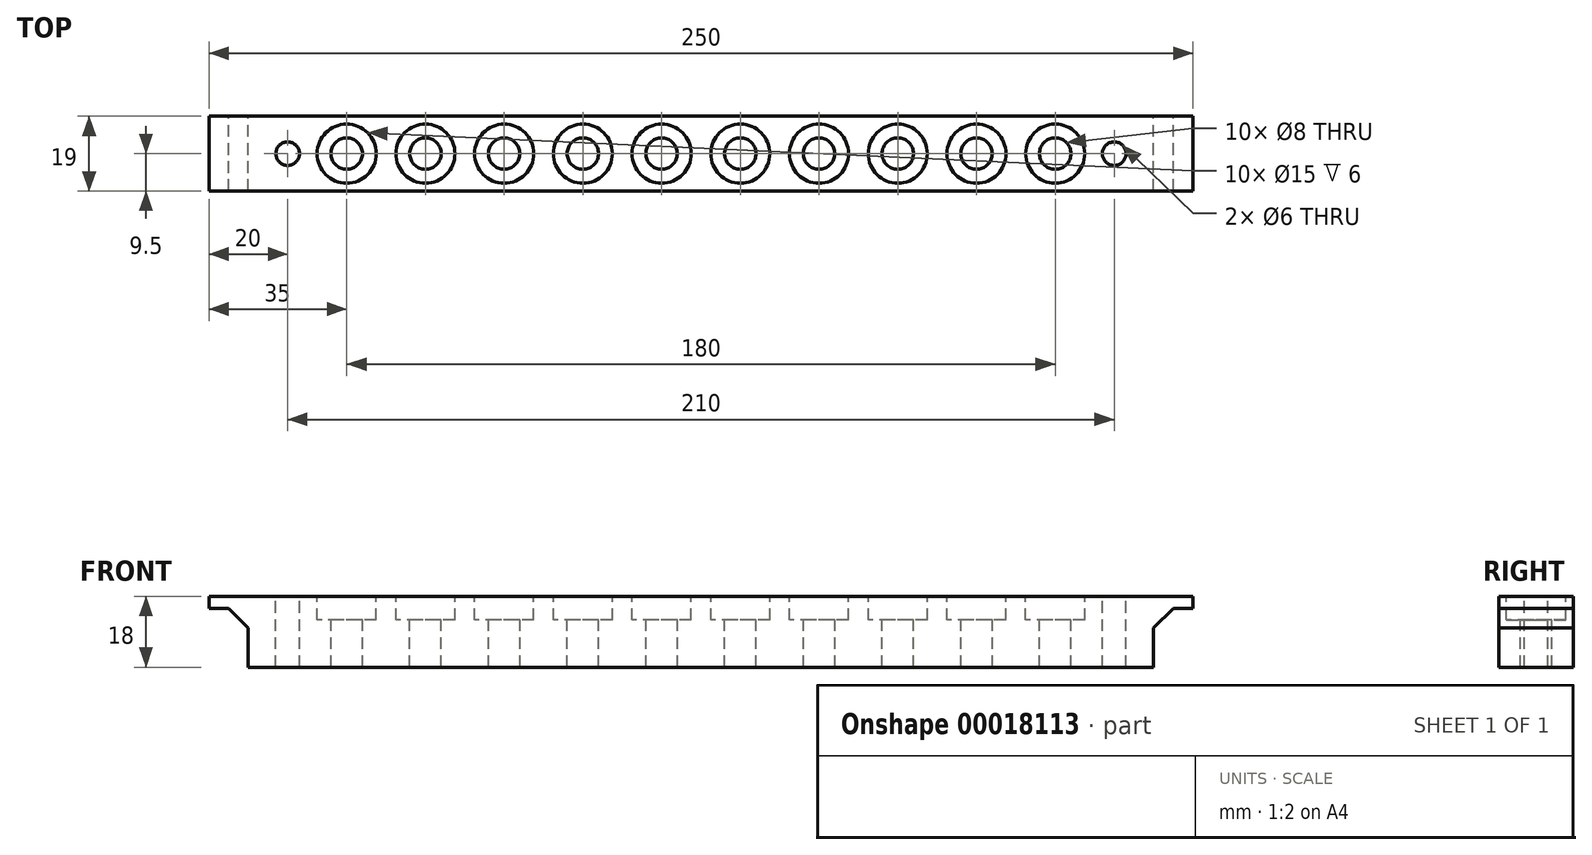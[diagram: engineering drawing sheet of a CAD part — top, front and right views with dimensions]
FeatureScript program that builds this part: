
annotation { "Feature Type Name" : "Feature", "Feature Type Description" : "" }
export const myFeature = defineFeature(function(context is Context, id is Id, definition is map)
    precondition{}
    {
        {
            var Q0;
            Q0=qCreatedBy(makeId("Front.planeOp"),FACE);
            var sketch = newSketch(context, id + "F0", { "sketchPlane" : qUnion([Q0])});
            skLineSegment(sketch, "E0", {"start": v(-125, 9) * mm, "end": v(125, 9) * mm});
            skLineSegment(sketch, "E1", {"start": v(125, 9) * mm, "end": v(125, 6) * mm});
            skLineSegment(sketch, "E2", {"start": v(125, 6) * mm, "end": v(120, 6) * mm});
            skLineSegment(sketch, "E3", {"start": v(115, 1) * mm, "end": v(115, -9) * mm});
            skLineSegment(sketch, "E4", {"start": v(115, -9) * mm, "end": v(-115, -9) * mm});
            skLineSegment(sketch, "E5", {"start": v(120, 6) * mm, "end": v(115, 1) * mm});
            skLineSegment(sketch, "E6", {"start": v(-125, 9) * mm, "end": v(-125, 6) * mm});
            skLineSegment(sketch, "E7", {"start": v(-125, 6) * mm, "end": v(-120, 6) * mm});
            skLineSegment(sketch, "E8", {"start": v(-115, 1) * mm, "end": v(-115, -9) * mm});
            skLineSegment(sketch, "E9", {"start": v(-120, 6) * mm, "end": v(-115, 1) * mm});
            skSolve(sketch);
        }
        {
            var Q0;
            Q0 = qSketchRegion(id + "F0", true);
            extrude(context, id + "F1", {"entities" : qUnion([Q0]), "endBound" : BoundingType.SYMMETRIC, "depth" : 19 * mm});
        }
        {
            var Q0;
            Q0=makeQuery(id+"F1.opExtrude","SWEPT_BODY",BODY,{"disambiguationData":[OSD([sQuery(id+"F0.wireOp",EDGE,"E0"),sQuery(id+"F0.wireOp",EDGE,"E1"),sQuery(id+"F0.wireOp",EDGE,"E2"),sQuery(id+"F0.wireOp",EDGE,"E3"),sQuery(id+"F0.wireOp",EDGE,"E4"),sQuery(id+"F0.wireOp",EDGE,"E5"),sQuery(id+"F0.wireOp",EDGE,"E6"),sQuery(id+"F0.wireOp",EDGE,"E7"),sQuery(id+"F0.wireOp",EDGE,"E8"),sQuery(id+"F0.wireOp",EDGE,"E9")])]});
            transform(context, id + "F2", {"entities" : qUnion([Q0]), "transformType" : TransformType.TRANSLATION_3D, "dx" : 125 * mm, "dy" : 0 * mm, "dz" : 0 * mm, "makeCopy" : false});
        }
        {
            var Q0;
            Q0=makeQuery(id+"F1.opExtrude","SWEPT_FACE",FACE,{"disambiguationData":[OSD([sQuery(id+"F0.wireOp",EDGE,"E0")])]});
            var sketch = newSketch(context, id + "F3", { "sketchPlane" : qUnion([Q0])});
            skLineSegment(sketch, "E10.0", {"start": v(20, -9.5) * mm, "end": v(20, 9.5) * mm, "construction": true});
            skLineSegment(sketch, "E11", {"start": v(-2.51, 0) * mm, "end": v(250, 0) * mm, "construction": true});
            skLineSegment(sketch, "E12.0", {"start": v(230, -9.5) * mm, "end": v(230, 9.5) * mm, "construction": true});
            skLineSegment(sketch, "E13.0", {"start": v(35, -9.5) * mm, "end": v(35, 9.5) * mm, "construction": true});
            skPoint(sketch, "E14", {"position": v(20, 0) * mm});
            skPoint(sketch, "E15", {"position": v(35, 0) * mm});
            skPoint(sketch, "E16", {"position": v(230, 0) * mm});
            skLineSegment(sketch, "E17.1.0.0", {"start": v(55, -9.5) * mm, "end": v(55, 9.5) * mm, "construction": true});
            skPoint(sketch, "E17.1.0.1", {"position": v(55, 0) * mm});
            skLineSegment(sketch, "E17.2.0.0", {"start": v(75, -9.5) * mm, "end": v(75, 9.5) * mm, "construction": true});
            skPoint(sketch, "E17.2.0.1", {"position": v(75, 0) * mm});
            skLineSegment(sketch, "E17.3.0.0", {"start": v(95, -9.5) * mm, "end": v(95, 9.5) * mm, "construction": true});
            skPoint(sketch, "E17.3.0.1", {"position": v(95, 0) * mm});
            skLineSegment(sketch, "E17.4.0.0", {"start": v(115, -9.5) * mm, "end": v(115, 9.5) * mm, "construction": true});
            skPoint(sketch, "E17.4.0.1", {"position": v(115, 0) * mm});
            skLineSegment(sketch, "E17.5.0.0", {"start": v(135, -9.5) * mm, "end": v(135, 9.5) * mm, "construction": true});
            skPoint(sketch, "E17.5.0.1", {"position": v(135, 0) * mm});
            skLineSegment(sketch, "E17.6.0.0", {"start": v(155, -9.5) * mm, "end": v(155, 9.5) * mm, "construction": true});
            skPoint(sketch, "E17.6.0.1", {"position": v(155, 0) * mm});
            skLineSegment(sketch, "E17.7.0.0", {"start": v(175, -9.5) * mm, "end": v(175, 9.5) * mm, "construction": true});
            skPoint(sketch, "E17.7.0.1", {"position": v(175, 0) * mm});
            skLineSegment(sketch, "E17.8.0.0", {"start": v(195, -9.5) * mm, "end": v(195, 9.5) * mm, "construction": true});
            skPoint(sketch, "E17.8.0.1", {"position": v(195, 0) * mm});
            skLineSegment(sketch, "E17.9.0.0", {"start": v(215, -9.5) * mm, "end": v(215, 9.5) * mm, "construction": true});
            skPoint(sketch, "E17.9.0.1", {"position": v(215, 0) * mm});
            skLineSegment(sketch, "E17.direction1", {"start": v(35, -9.5) * mm, "end": v(55, -9.5) * mm, "construction": true});
            skSolve(sketch);
        }
        {
            var Q0;
            Q0=sQuery(id+"F3.wireOp",VERTEX,"E15");
            var Q1;
            Q1=sQuery(id+"F3.wireOp",VERTEX,"E17.1.0.1");
            var Q2;
            Q2=sQuery(id+"F3.wireOp",VERTEX,"E17.2.0.1");
            var Q3;
            Q3=sQuery(id+"F3.wireOp",VERTEX,"E17.3.0.1");
            var Q4;
            Q4=sQuery(id+"F3.wireOp",VERTEX,"E17.4.0.1");
            var Q5;
            Q5=sQuery(id+"F3.wireOp",VERTEX,"E17.5.0.1");
            var Q6;
            Q6=sQuery(id+"F3.wireOp",VERTEX,"E17.6.0.1");
            var Q7;
            Q7=sQuery(id+"F3.wireOp",VERTEX,"E17.7.0.1");
            var Q8;
            Q8=sQuery(id+"F3.wireOp",VERTEX,"E17.8.0.1");
            var Q9;
            Q9=sQuery(id+"F3.wireOp",VERTEX,"E17.9.0.1");
            var Q10;
            Q10=makeQuery(id+"F1.opExtrude","SWEPT_BODY",BODY,{"disambiguationData":[OSD([sQuery(id+"F0.wireOp",EDGE,"E0"),sQuery(id+"F0.wireOp",EDGE,"E1"),sQuery(id+"F0.wireOp",EDGE,"E2"),sQuery(id+"F0.wireOp",EDGE,"E3"),sQuery(id+"F0.wireOp",EDGE,"E4"),sQuery(id+"F0.wireOp",EDGE,"E5"),sQuery(id+"F0.wireOp",EDGE,"E6"),sQuery(id+"F0.wireOp",EDGE,"E7"),sQuery(id+"F0.wireOp",EDGE,"E8"),sQuery(id+"F0.wireOp",EDGE,"E9")])]});
            hole(context, id + "F4", {"style" : HoleStyle.C_BORE, "holeDiameter" : 8 * mm, "cBoreDiameter" : 15 * mm, "cBoreDepth" : 6 * mm, "endStyle" : HoleEndStyle.THROUGH, "locations" : qUnion([Q0, Q1, Q2, Q3, Q4, Q5, Q6, Q7, Q8, Q9]), "scope" : qUnion([Q10])});
        }
        {
            var Q0;
            Q0=sQuery(id+"F3.wireOp",VERTEX,"E14");
            var Q1;
            Q1=sQuery(id+"F3.wireOp",VERTEX,"E16");
            var Q2;
            Q2=makeQuery(id+"F1.opExtrude","SWEPT_BODY",BODY,{"disambiguationData":[OSD([sQuery(id+"F0.wireOp",EDGE,"E0"),sQuery(id+"F0.wireOp",EDGE,"E1"),sQuery(id+"F0.wireOp",EDGE,"E2"),sQuery(id+"F0.wireOp",EDGE,"E3"),sQuery(id+"F0.wireOp",EDGE,"E4"),sQuery(id+"F0.wireOp",EDGE,"E5"),sQuery(id+"F0.wireOp",EDGE,"E6"),sQuery(id+"F0.wireOp",EDGE,"E7"),sQuery(id+"F0.wireOp",EDGE,"E8"),sQuery(id+"F0.wireOp",EDGE,"E9")])]});
            hole(context, id + "F5", {"style" : HoleStyle.SIMPLE, "holeDiameter" : 6 * mm, "endStyle" : HoleEndStyle.THROUGH, "locations" : qUnion([Q0, Q1]), "scope" : qUnion([Q2])});
        }
        {
            var Q0;
            Q0=makeQuery(id+"F1.opExtrude","SWEPT_BODY",BODY,{"disambiguationData":[OSD([sQuery(id+"F0.wireOp",EDGE,"E0"),sQuery(id+"F0.wireOp",EDGE,"E1"),sQuery(id+"F0.wireOp",EDGE,"E2"),sQuery(id+"F0.wireOp",EDGE,"E3"),sQuery(id+"F0.wireOp",EDGE,"E4"),sQuery(id+"F0.wireOp",EDGE,"E5"),sQuery(id+"F0.wireOp",EDGE,"E6"),sQuery(id+"F0.wireOp",EDGE,"E7"),sQuery(id+"F0.wireOp",EDGE,"E8"),sQuery(id+"F0.wireOp",EDGE,"E9")])]});
            transform(context, id + "F6", {"entities" : qUnion([Q0]), "transformType" : TransformType.TRANSLATION_3D, "dx" : 0 * mm, "dy" : 0 * mm, "dz" : -3 * mm, "makeCopy" : false});
        }
        {
            var Q0;
            Q0=makeQuery(id+"F1.opExtrude","SWEPT_BODY",BODY,{"disambiguationData":[OSD([sQuery(id+"F0.wireOp",EDGE,"E0"),sQuery(id+"F0.wireOp",EDGE,"E1"),sQuery(id+"F0.wireOp",EDGE,"E2"),sQuery(id+"F0.wireOp",EDGE,"E3"),sQuery(id+"F0.wireOp",EDGE,"E4"),sQuery(id+"F0.wireOp",EDGE,"E5"),sQuery(id+"F0.wireOp",EDGE,"E6"),sQuery(id+"F0.wireOp",EDGE,"E7"),sQuery(id+"F0.wireOp",EDGE,"E8"),sQuery(id+"F0.wireOp",EDGE,"E9")])]});
            transform(context, id + "F7", {"entities" : qUnion([Q0]), "transformType" : TransformType.TRANSLATION_3D, "dx" : -35 * mm, "dy" : 0 * mm, "dz" : 0 * mm, "makeCopy" : false});
        }
    });
